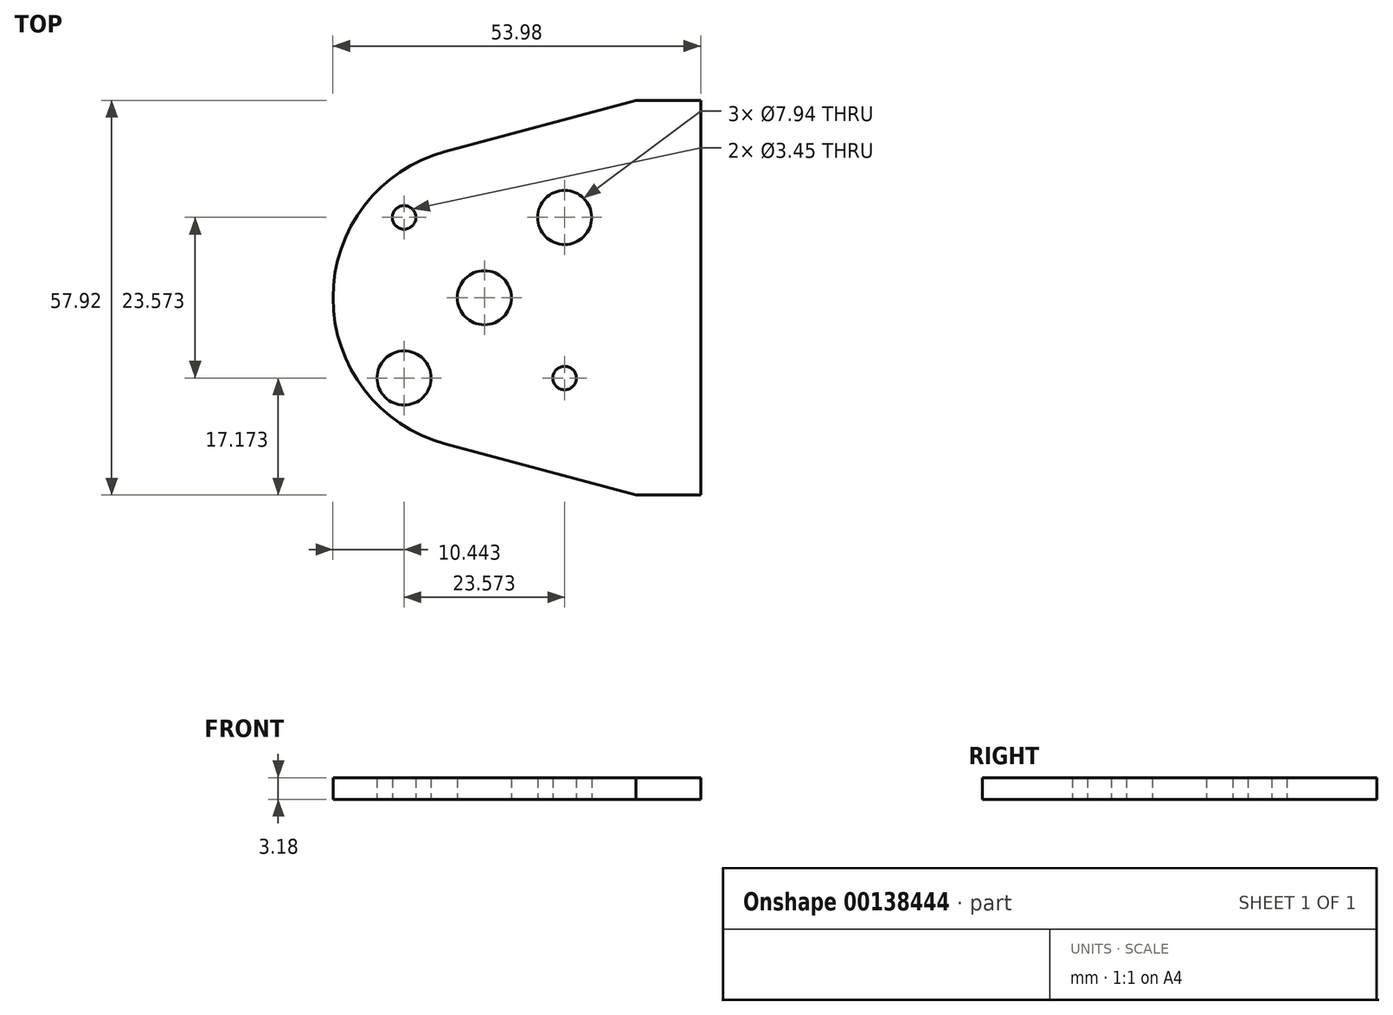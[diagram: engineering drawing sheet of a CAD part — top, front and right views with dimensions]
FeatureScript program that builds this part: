
annotation { "Feature Type Name" : "Feature", "Feature Type Description" : "" }
export const myFeature = defineFeature(function(context is Context, id is Id, definition is map)
    precondition{}
    {
        {
            var Q0;
            Q0=qCreatedBy(makeId("Top.planeOp"),FACE);
            var sketch = newSketch(context, id + "F0", { "sketchPlane" : qUnion([Q0])});
            skCircle(sketch, "E0", {"center": v(0, 0) * mm, "radius": 3.97 * mm});
            skLineSegment(sketch, "E1.bottom", {"start": v(-11.79, 11.79) * mm, "end": v(11.79, 11.79) * mm, "construction": true});
            skLineSegment(sketch, "E1.top", {"start": v(-11.79, -11.79) * mm, "end": v(11.79, -11.79) * mm, "construction": true});
            skLineSegment(sketch, "E1.left", {"start": v(-11.79, 11.79) * mm, "end": v(-11.79, -11.79) * mm, "construction": true});
            skLineSegment(sketch, "E1.right", {"start": v(11.79, 11.79) * mm, "end": v(11.79, -11.79) * mm, "construction": true});
            skCircle(sketch, "E2", {"center": v(0, 0) * mm, "radius": 11.11 * mm, "construction": true});
            skCircle(sketch, "E3", {"center": v(-11.79, 11.79) * mm, "radius": 5.56 * mm, "construction": true});
            skCircle(sketch, "E4", {"center": v(-11.79, 11.79) * mm, "radius": 1.73 * mm});
            skCircle(sketch, "E5", {"center": v(11.79, 11.79) * mm, "radius": 3.97 * mm});
            skCircle(sketch, "E6", {"center": v(-11.79, -11.79) * mm, "radius": 3.97 * mm});
            skCircle(sketch, "E7", {"center": v(11.79, -11.79) * mm, "radius": 1.73 * mm});
            skLineSegment(sketch, "E8", {"start": v(0, 0) * mm, "end": v(22.23, 0) * mm, "construction": true});
            skLineSegment(sketch, "E9.bottom", {"start": v(22.23, 28.96) * mm, "end": v(31.75, 28.96) * mm});
            skLineSegment(sketch, "E9.top", {"start": v(22.23, -28.96) * mm, "end": v(31.75, -28.96) * mm});
            skLineSegment(sketch, "E9.left", {"start": v(22.23, 28.96) * mm, "end": v(22.23, -28.96) * mm, "construction": true});
            skLineSegment(sketch, "E9.right", {"start": v(31.75, 28.96) * mm, "end": v(31.75, -28.96) * mm});
            skArc(sketch, "E10", {"start": v(-5.75, 21.47) * mm, "mid": v(-22.22, 0) * mm, "end": v(-5.75, -21.47) * mm});
            skLineSegment(sketch, "E11", {"start": v(-5.75, 21.47) * mm, "end": v(22.23, 28.96) * mm});
            skLineSegment(sketch, "E12", {"start": v(-5.75, -21.47) * mm, "end": v(22.23, -28.96) * mm});
            skLineSegment(sketch, "E13", {"start": v(-5.75, 21.47) * mm, "end": v(8.24, 21.47) * mm, "construction": true});
            skLineSegment(sketch, "E14", {"start": v(8.24, 21.47) * mm, "end": v(8.24, 25.22) * mm, "construction": true});
            skSolve(sketch);
        }
        {
            var Q0;
            Q0=qSketchRegion(id+"F0",true);
            extrude(context, id + "F1", {"entities" : qUnion([Q0]), "depth" : 3.17 * mm});
        }
    });
